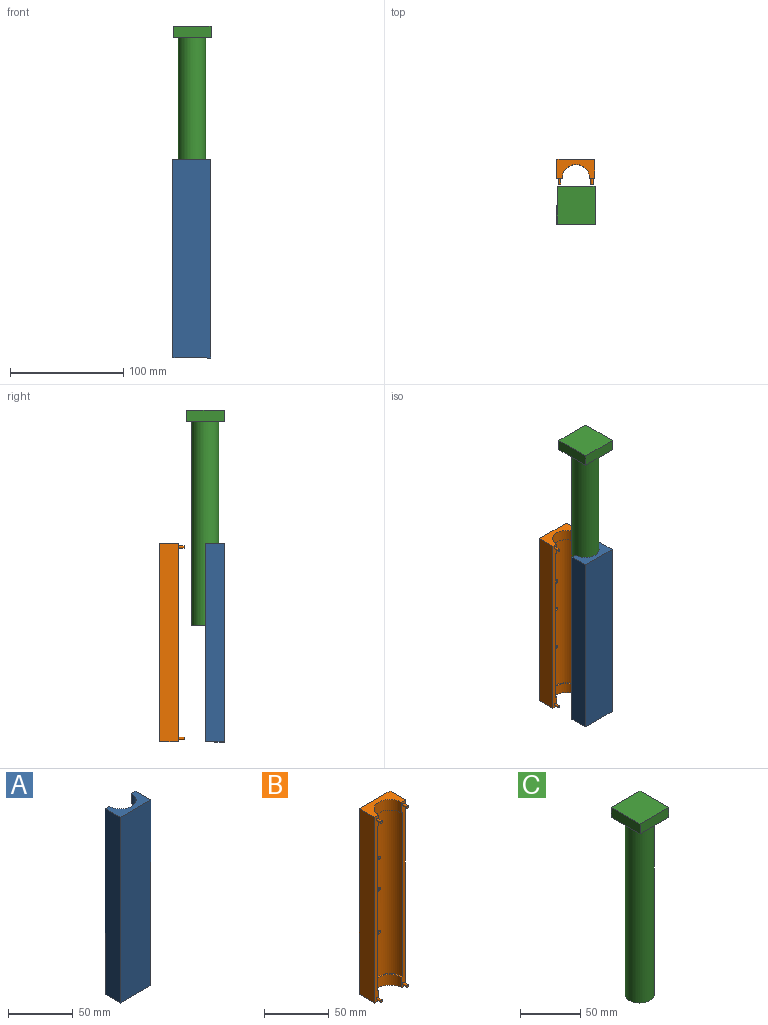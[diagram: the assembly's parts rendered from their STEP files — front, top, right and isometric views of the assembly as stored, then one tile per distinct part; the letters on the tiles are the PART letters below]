
ASSEMBLY  parts=3 mates=3
PART A: 20 faces, bbox 33.4x16.7x175 mm
  f0: plane 175x4.5mm, normal (0,1,0), area 622.7mm2, adj f4,f5,f6,f7,f8,f9,f10,f11
  f1: plane 175x4.5mm, normal (0,1,0), area 622.7mm2, adj f2,f5,f6,f7,f8,f9,f10,f11
  f2: plane 175x16.7mm, normal (-1,0,0), area 2922.5mm2, adj f1,f3,f5,f9
  f3: plane 175x33.4mm, normal (0,-1,0), area 5845mm2, adj f2,f4,f5,f9
  f4: plane 175x16.7mm, normal (1,0,0), area 2922.5mm2, adj f0,f3,f5,f9
  f5: plane 33.4x16.7mm, normal (0,0,1), area 324mm2, adj f0,f1,f2,f3,f4,f11
  f6: plane 26.4x13.2mm, normal (0,0,-1), area 39.9mm2, adj f0,f1,f7,f11
  f7: cylinder r=13.2mm len=155mm, axis (0,0,1), area 6427.7mm2, adj f0,f1,f6,f8
  f8: plane 26.4x13.2mm, normal (0,0,1), area 39.9mm2, adj f0,f1,f7,f10
  f9: plane 33.4x16.7mm, normal (0,0,-1), area 324mm2, adj f0,f1,f2,f3,f4,f10
  f10: cylinder r=12.2mm len=24.4mm, axis (0,0,-1), area 383.3mm2, adj f0,f1,f8,f9
  f11: cylinder r=12.2mm len=24.4mm, axis (0,0,-1), area 383.3mm2, adj f0,f1,f5,f6
  f12: cylinder r=1.25mm len=6mm, axis (0,1,0), area 47.1mm2, adj f1,f13
  f13: plane 2.5x2.5mm, normal (0,1,0), area 4.9mm2, adj f12
  f14: cylinder r=1.25mm len=6mm, axis (0,1,0), area 47.1mm2, adj f1,f15
  f15: plane 2.5x2.5mm, normal (0,1,0), area 4.9mm2, adj f14
  f16: cylinder r=1.25mm len=6mm, axis (0,1,0), area 47.1mm2, adj f0,f17
  f17: plane 2.5x2.5mm, normal (0,1,0), area 4.9mm2, adj f16
  f18: cylinder r=1.25mm len=6mm, axis (0,1,0), area 47.1mm2, adj f0,f19
  f19: plane 2.5x2.5mm, normal (0,1,0), area 4.9mm2, adj f18
PART B: 26 faces, bbox 33.4x21.7x175 mm
  f0: plane 175x4.5mm, normal (0,-1,0), area 626.2mm2, adj f4,f5,f6,f7,f8,f9,f10,f11
  f1: plane 175x4.5mm, normal (0,-1,0), area 626.2mm2, adj f2,f5,f6,f7,f8,f9,f10,f11
  f2: plane 175x16.7mm, normal (-1,0,0), area 2922.5mm2, adj f1,f3,f5,f9
  f3: plane 175x33.4mm, normal (0,1,0), area 5729.5mm2, adj f2,f4,f5,f9,f23,f24,f25
  f4: plane 175x16.7mm, normal (1,0,0), area 2922.5mm2, adj f0,f3,f5,f9
  f5: plane 33.4x16.7mm, normal (0,0,1), area 324mm2, adj f0,f1,f2,f3,f4,f11
  f6: plane 26.4x13.2mm, normal (0,0,-1), area 39.9mm2, adj f0,f1,f7,f11
  f7: cylinder r=13.2mm len=155mm, axis (0,0,1), area 6406.4mm2, adj f0,f1,f6,f8,f20,f21,f22
  f8: plane 26.4x13.2mm, normal (0,0,1), area 39.9mm2, adj f0,f1,f7,f10
  f9: plane 33.4x16.7mm, normal (0,0,-1), area 324mm2, adj f0,f1,f2,f3,f4,f10
  f10: cylinder r=12.2mm len=24.4mm, axis (0,0,-1), area 383.3mm2, adj f0,f1,f8,f9
  f11: cylinder r=12.2mm len=24.4mm, axis (0,0,-1), area 383.3mm2, adj f0,f1,f5,f6
  f12: cylinder r=1mm len=5mm, axis (0,1,0), area 31.4mm2, adj f0,f13
  f13: plane 2x2mm, normal (0,-1,0), area 3.1mm2, adj f12
  f14: cylinder r=1mm len=5mm, axis (0,1,0), area 31.4mm2, adj f0,f15
  f15: plane 2x2mm, normal (0,-1,0), area 3.1mm2, adj f14
  f16: cylinder r=1mm len=5mm, axis (0,1,0), area 31.4mm2, adj f1,f17
  f17: plane 2x2mm, normal (0,-1,0), area 3.1mm2, adj f16
  f18: cylinder r=1mm len=5mm, axis (0,1,0), area 31.4mm2, adj f1,f19
  f19: plane 2x2mm, normal (0,-1,0), area 3.1mm2, adj f18
  f20: cylinder r=1.5mm len=3mm, axis (0,1,0), area 14.8mm2, adj f7,f23
  f21: cylinder r=1.5mm len=3mm, axis (0,1,0), area 14.8mm2, adj f7,f25
  f22: cylinder r=1.5mm len=3mm, axis (0,1,0), area 14.8mm2, adj f7,f24
  f23: cone r=1.5mm half-angle=45deg, axis (0,1,0), area 44.4mm2, adj f3,f20
  f24: cone r=1.5mm half-angle=45deg, axis (0,1,0), area 44.4mm2, adj f3,f22
  f25: cone r=1.5mm half-angle=45deg, axis (0,1,0), area 44.4mm2, adj f3,f21
PART C: 8 faces, bbox 33.4x33.4x190 mm
  f0: cylinder r=12mm len=180mm, axis (0,0,1), area 13571.7mm2, adj f1,f7
  f1: plane 24x24mm, normal (0,0,-1), area 452.4mm2, adj f0
  f2: plane 33.4x10mm, normal (-1,0,0), area 334mm2, adj f3,f5,f6,f7
  f3: plane 33.4x10mm, normal (0,-1,0), area 334mm2, adj f2,f4,f6,f7
  f4: plane 33.4x10mm, normal (1,0,0), area 334mm2, adj f3,f5,f6,f7
  f5: plane 33.4x10mm, normal (0,1,0), area 334mm2, adj f2,f4,f6,f7
  f6: plane 33.4x33.4mm, normal (0,0,1), area 1115.6mm2, adj f2,f3,f4,f5
  f7: plane 33.4x33.4mm, normal (0,0,-1), area 663.2mm2, adj f0,f2,f3,f4,f5
PLACE A t=(-8.53,-23.29,-148.36)mm
PLACE B t=(-8.53,0.42,-148.36)mm
PLACE C t=(-8.37,-23.5,-40.56)mm
MATE parallel A.f0 <-> B.f0  axis (0,1,0) through (21.06,-37.99,-75.86)mm
MATE slider C.f0 <-> A.f7  axis (0,0,1) through (6.17,-37.99,29.44)mm
MATE slider B.f16 <-> A.f12  axis (0,1,0) through (-8.03,-16.78,8.64)mm
